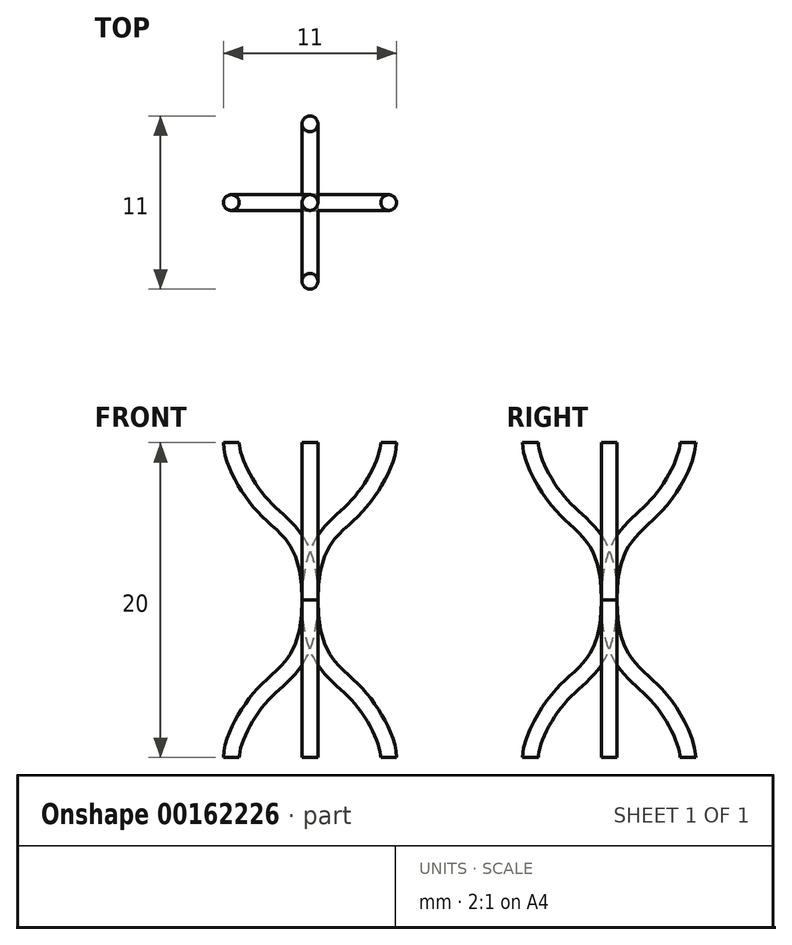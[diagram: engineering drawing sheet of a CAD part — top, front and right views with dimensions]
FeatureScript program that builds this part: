
annotation { "Feature Type Name" : "Feature", "Feature Type Description" : "" }
export const myFeature = defineFeature(function(context is Context, id is Id, definition is map)
    precondition{}
    {
        {
            var Q0;
            Q0=qCreatedBy(makeId("Front.planeOp"),FACE);
            var sketch = newSketch(context, id + "F0", { "sketchPlane" : qUnion([Q0])});
            skFitSpline(sketch, "E0", {"points": [v(-5, 0) * mm, v(-3, 4) * mm, v(0, 10) * mm], "startDerivative": vector(0, 6.67) * mm, "endDerivative": vector(0, 21.8) * mm});
            skFitSpline(sketch, "E1.MirrorCS", {"points": [v(-5, 0) * mm, v(-3, -4) * mm, v(0, -10) * mm], "startDerivative": vector(0, -6.67) * mm, "endDerivative": vector(0, -21.8) * mm});
            skSolve(sketch);
        }
        {
            var Q0;
            Q0=qCreatedBy(makeId("Top.planeOp"),FACE);
            var sketch = newSketch(context, id + "F1", { "sketchPlane" : qUnion([Q0])});
            skCircle(sketch, "E2", {"center": v(-5, 0) * mm, "radius": 0.5 * mm});
            skSolve(sketch);
        }
        {
            var Q0;
            Q0 = qSketchRegion(id + "F1", true);
            var Q1;
            Q1=sQuery(id+"F0.wireOp",EDGE,"E0");
            sweep(context, id + "F2", {"profiles" : qUnion([Q0]), "path" : qUnion([Q1])});
        }
        {
            var Q0;
            Q0=qCreatedBy(makeId("Right.planeOp"),FACE);
            var sketch = newSketch(context, id + "F3", { "sketchPlane" : qUnion([Q0])});
            skLineSegment(sketch, "E3", {"start": v(0, 103.56) * mm, "end": v(0, -95.8) * mm, "construction": true});
            skSolve(sketch);
        }
        {
            var Q0;
            Q0=makeQuery(id+"F2.opSweep","SWEPT_BODY",BODY,{"disambiguationData":[OSD([sQuery(id+"F0.wireOp",EDGE,"E0"),sQuery(id+"F1.wireOp",EDGE,"E2")])]});
            var Q1;
            Q1=sQuery(id+"F3.wireOp",EDGE,"E3");
            circularPattern(context, id + "F4", {"entities" : qUnion([Q0]), "axis" : qUnion([Q1]), "angle" : 360 * degree, "instanceCount" : 4, "equalSpace" : true});
        }
        {
            var Q0;
            Q0=makeQuery(id+"F4.opPattern","COPY",BODY,{"derivedFrom":makeQuery(id+"F2.opSweep","SWEPT_BODY",BODY,{"disambiguationData":[OSD([sQuery(id+"F0.wireOp",EDGE,"E0"),sQuery(id+"F1.wireOp",EDGE,"E2")])]}),"instanceName":"2"});
            var Q1;
            Q1=makeQuery(id+"F4.opPattern","COPY",BODY,{"derivedFrom":makeQuery(id+"F2.opSweep","SWEPT_BODY",BODY,{"disambiguationData":[OSD([sQuery(id+"F0.wireOp",EDGE,"E0"),sQuery(id+"F1.wireOp",EDGE,"E2")])]}),"instanceName":"1"});
            var Q2;
            Q2=makeQuery(id+"F2.opSweep","SWEPT_BODY",BODY,{"disambiguationData":[OSD([sQuery(id+"F0.wireOp",EDGE,"E0"),sQuery(id+"F1.wireOp",EDGE,"E2")])]});
            var Q3;
            Q3=makeQuery(id+"F4.opPattern","COPY",BODY,{"derivedFrom":makeQuery(id+"F2.opSweep","SWEPT_BODY",BODY,{"disambiguationData":[OSD([sQuery(id+"F0.wireOp",EDGE,"E0"),sQuery(id+"F1.wireOp",EDGE,"E2")])]}),"instanceName":"3"});
            var Q4;
            Q4=makeQuery(id+"F4.opPattern","COPY",FACE,{"derivedFrom":makeQuery(id+"F2.opSweep","CAP_FACE",FACE,{"disambiguationData":[OSD([sQuery(id+"F0.wireOp",VERTEX,"E0.end"),sQuery(id+"F1.wireOp",EDGE,"E2")])],"isStart":false}),"instanceName":"1"});
            mirror(context, id + "F5", {"entities" : qUnion([Q0, Q1, Q2, Q3]), "mirrorPlane" : qUnion([Q4])});
        }
    });
